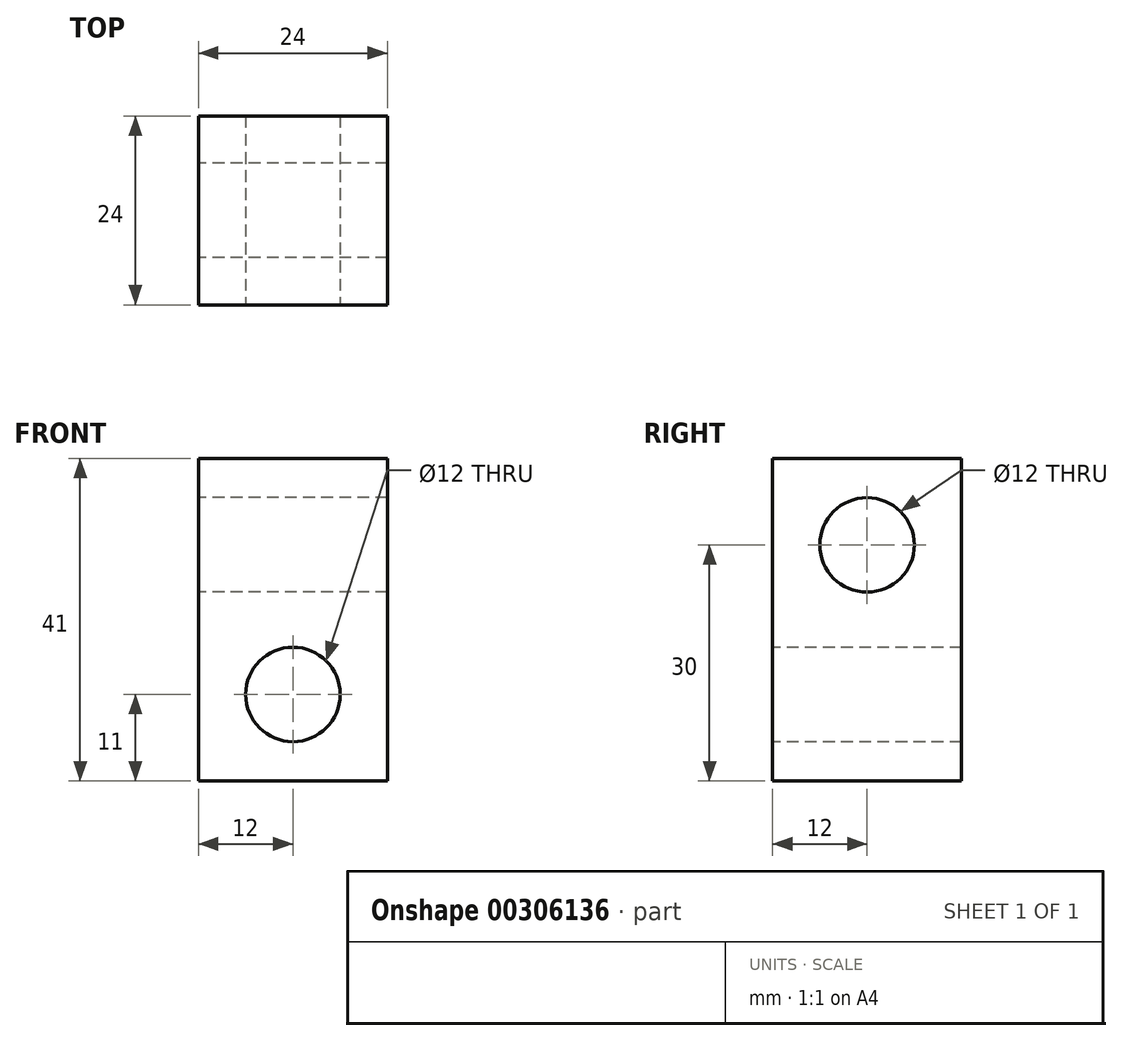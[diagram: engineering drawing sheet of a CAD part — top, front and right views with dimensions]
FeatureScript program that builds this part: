
annotation { "Feature Type Name" : "Feature", "Feature Type Description" : "" }
export const myFeature = defineFeature(function(context is Context, id is Id, definition is map)
    precondition{}
    {
        {
            var Q0;
            Q0=qCreatedBy(makeId("Top.planeOp"),FACE);
            var sketch = newSketch(context, id + "F0", { "sketchPlane" : qUnion([Q0])});
            skLineSegment(sketch, "E0.bottom", {"start": v(0, 0) * mm, "end": v(24, 0) * mm});
            skLineSegment(sketch, "E0.top", {"start": v(0, 24) * mm, "end": v(24, 24) * mm});
            skLineSegment(sketch, "E0.left", {"start": v(0, 0) * mm, "end": v(0, 24) * mm});
            skLineSegment(sketch, "E0.right", {"start": v(24, 0) * mm, "end": v(24, 24) * mm});
            skSolve(sketch);
        }
        {
            var Q0;
            Q0=makeQuery(id+"F0.imprint","IMPRINT",FACE,{"disambiguationData":[TD([[makeQuery(id+"F0.imprint","IMPRINT",EDGE,{"derivedFrom":sQuery(id+"F0.wireOp",EDGE,"E0.bottom")}),1.0]])]});
            extrude(context, id + "F1", {"entities" : qUnion([Q0]), "depth" : 41 * mm});
        }
        {
            var Q0;
            Q0=makeQuery(id+"F1.opExtrude","SWEPT_FACE",FACE,{"disambiguationData":[OSD([sQuery(id+"F0.wireOp",EDGE,"E0.bottom")])]});
            var sketch = newSketch(context, id + "F2", { "sketchPlane" : qUnion([Q0])});
            skCircle(sketch, "E1", {"center": v(12, 11) * mm, "radius": 6 * mm});
            skSolve(sketch);
        }
        {
            var Q0;
            Q0=makeQuery(id+"F2.imprint","IMPRINT",FACE,{"disambiguationData":[TD([[makeQuery(id+"F2.imprint","IMPRINT",EDGE,{"derivedFrom":sQuery(id+"F2.wireOp",EDGE,"E1")}),1.0]])]});
            extrude(context, id + "F3", {"entities" : qUnion([Q0]), "operationType" : NewBodyOperationType.REMOVE, "oppositeDirection" : true, "depth" : 25 * mm});
        }
        {
            var Q0;
            Q0=makeQuery(id+"F1.opExtrude","SWEPT_FACE",FACE,{"disambiguationData":[OSD([sQuery(id+"F0.wireOp",EDGE,"E0.left")])]});
            var sketch = newSketch(context, id + "F4", { "sketchPlane" : qUnion([Q0])});
            skCircle(sketch, "E2", {"center": v(-12, 30) * mm, "radius": 6 * mm});
            skSolve(sketch);
        }
        {
            var Q0;
            Q0=makeQuery(id+"F4.imprint","IMPRINT",FACE,{"disambiguationData":[TD([[makeQuery(id+"F4.imprint","IMPRINT",EDGE,{"derivedFrom":sQuery(id+"F4.wireOp",EDGE,"E2")}),1.0]])]});
            extrude(context, id + "F5", {"entities" : qUnion([Q0]), "operationType" : NewBodyOperationType.REMOVE, "oppositeDirection" : true, "depth" : 25 * mm});
        }
    });
